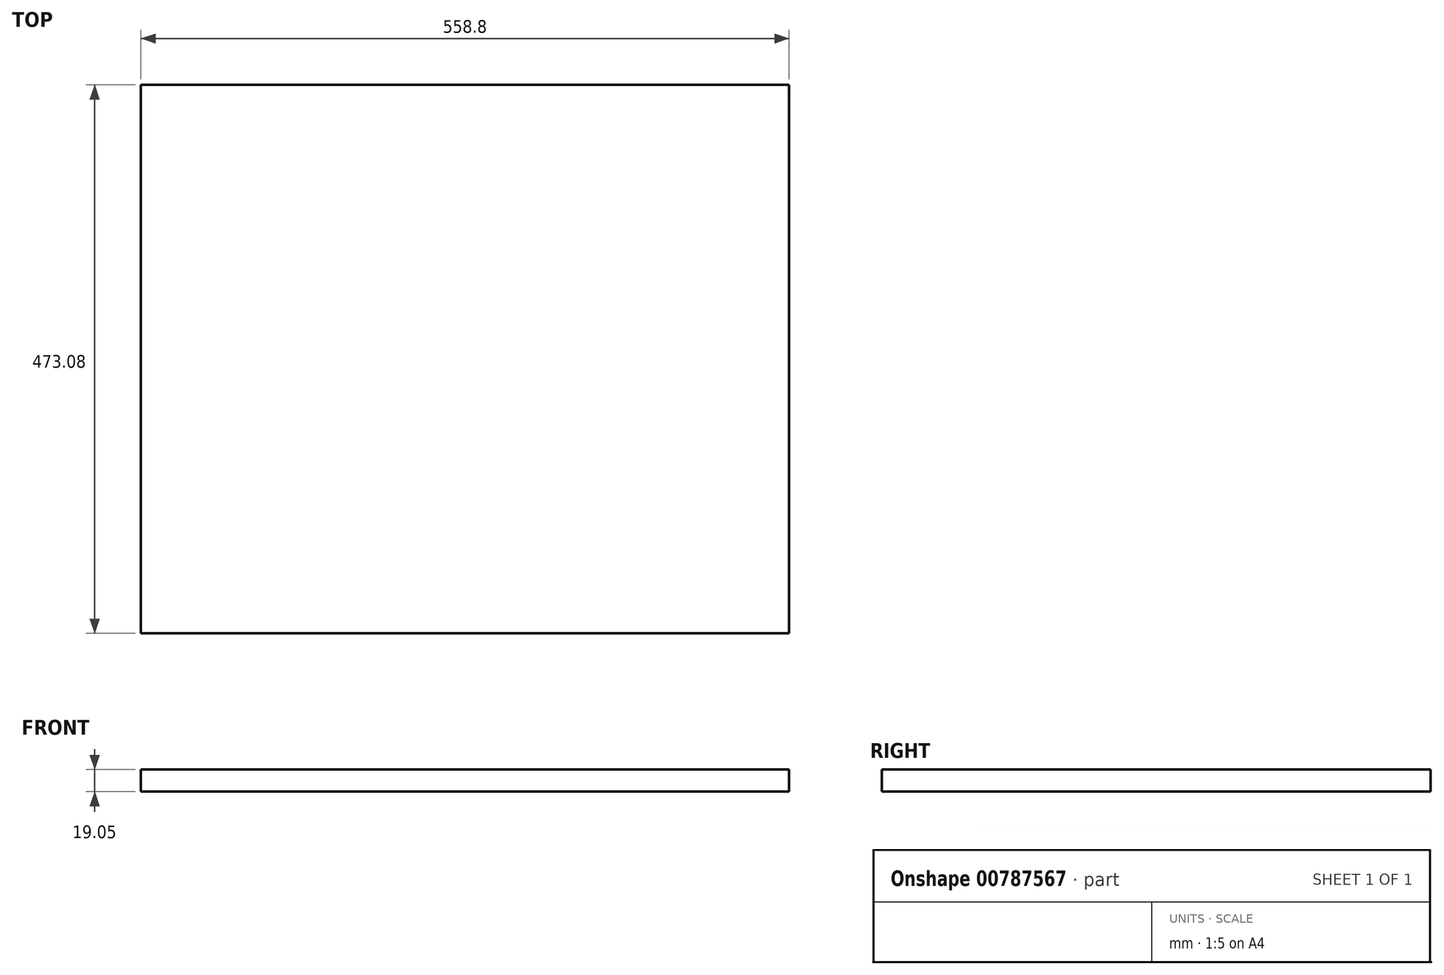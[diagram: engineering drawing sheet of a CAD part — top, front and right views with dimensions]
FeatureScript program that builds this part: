
annotation { "Feature Type Name" : "Feature", "Feature Type Description" : "" }
export const myFeature = defineFeature(function(context is Context, id is Id, definition is map)
    precondition{}
    {
        {
            var Q0;
            Q0=qCreatedBy(makeId("Top.planeOp"),FACE);
            var sketch = newSketch(context, id + "F0", { "sketchPlane" : qUnion([Q0])});
            skLineSegment(sketch, "E0.bottom", {"start": v(279.4, 236.54) * mm, "end": v(-279.4, 236.54) * mm});
            skLineSegment(sketch, "E0.top", {"start": v(279.4, -236.54) * mm, "end": v(-279.4, -236.54) * mm});
            skLineSegment(sketch, "E0.left", {"start": v(279.4, 236.54) * mm, "end": v(279.4, -236.54) * mm});
            skLineSegment(sketch, "E0.right", {"start": v(-279.4, 236.54) * mm, "end": v(-279.4, -236.54) * mm});
            skPoint(sketch, "E0.middle", {"position": v(0, 0) * mm});
            skSolve(sketch);
        }
        {
            var Q0;
            Q0 = qSketchRegion(id + "F0", true);
            extrude(context, id + "F1", {"entities" : qUnion([Q0]), "depth" : 19.05 * mm, "offsetDistance" : 25.4 * mm});
        }
    });
